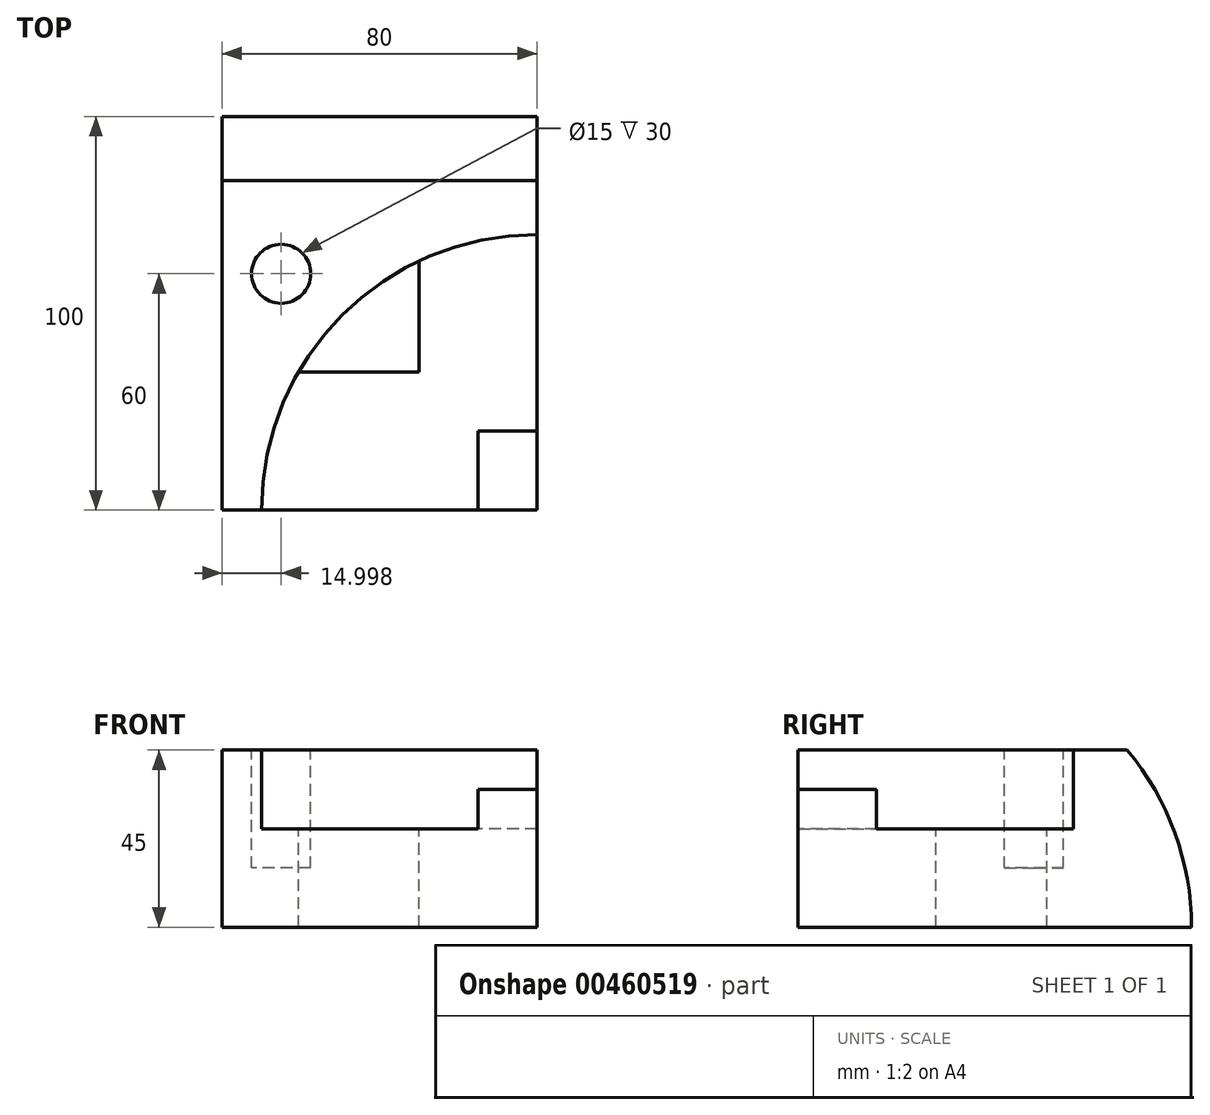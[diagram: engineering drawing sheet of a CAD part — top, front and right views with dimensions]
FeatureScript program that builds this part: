
annotation { "Feature Type Name" : "Feature", "Feature Type Description" : "" }
export const myFeature = defineFeature(function(context is Context, id is Id, definition is map)
    precondition{}
    {
        {
            var Q0;
            Q0=qCreatedBy(makeId("Front.planeOp"),FACE);
            var sketch = newSketch(context, id + "F0", { "sketchPlane" : qUnion([Q0])});
            skLineSegment(sketch, "E0.bottom", {"start": v(-52.62, 0) * mm, "end": v(27.38, 0) * mm});
            skLineSegment(sketch, "E0.top", {"start": v(-52.62, 45) * mm, "end": v(27.38, 45) * mm});
            skLineSegment(sketch, "E0.left", {"start": v(-52.62, 0) * mm, "end": v(-52.62, 45) * mm});
            skLineSegment(sketch, "E0.right", {"start": v(27.38, 0) * mm, "end": v(27.38, 45) * mm});
            skSolve(sketch);
        }
        {
            var Q0;
            Q0=makeQuery(id+"F0.imprint","IMPRINT",FACE,{"disambiguationData":[TD([[makeQuery(id+"F0.imprint","IMPRINT",EDGE,{"derivedFrom":sQuery(id+"F0.wireOp",EDGE,"E0.bottom")}),1.0]])]});
            extrude(context, id + "F1", {"entities" : qUnion([Q0]), "depth" : 100 * mm});
        }
        {
            var Q0;
            Q0=makeQuery(id+"F1.opExtrude","SWEPT_FACE",FACE,{"disambiguationData":[OSD([sQuery(id+"F0.wireOp",EDGE,"E0.right")])]});
            var sketch = newSketch(context, id + "F2", { "sketchPlane" : qUnion([Q0])});
            skLineSegment(sketch, "E1", {"start": v(0, 0) * mm, "end": v(-70, 0) * mm});
            skCircle(sketch, "E2", {"center": v(-70, 0) * mm, "radius": 70 * mm});
            skSolve(sketch);
        }
        {
            var Q0;
            {var subQ1=sQuery(id+"F0.wireOp",EDGE,"E0.right");var subQ2=makeQuery(id+"F1.opExtrude","CAP_EDGE",EDGE,{"disambiguationData":[OSD([subQ1])],"isStart":true});Q0=makeQuery(id+"F2.imprint","IMPRINT",FACE,{"disambiguationData":[TD([[makeQuery(id+"F2.imprint","IMPRINT",EDGE,{"derivedFrom":subQ2}),1.0]])]});}
            extrude(context, id + "F3", {"entities" : qUnion([Q0]), "operationType" : NewBodyOperationType.REMOVE, "oppositeDirection" : true, "depth" : 80 * mm});
        }
        {
            var Q0;
            Q0=makeQuery(id+"F1.opExtrude","SWEPT_FACE",FACE,{"disambiguationData":[OSD([sQuery(id+"F0.wireOp",EDGE,"E0.top")])]});
            var sketch = newSketch(context, id + "F4", { "sketchPlane" : qUnion([Q0])});
            skLineSegment(sketch, "E3", {"start": v(27.38, -100) * mm, "end": v(27.38, -30) * mm});
            skCircle(sketch, "E4", {"center": v(27.38, -100) * mm, "radius": 70 * mm});
            skSolve(sketch);
        }
        {
            var Q0;
            {var subQ0=sQuery(id+"F4.wireOp",EDGE,"E3");Q0=makeQuery(id+"F4.imprint","IMPRINT",FACE,{"disambiguationData":[TD([[makeQuery(id+"F4.imprint","IMPRINT",EDGE,{"derivedFrom":subQ0}),1.0]])]});}
            extrude(context, id + "F5", {"entities" : qUnion([Q0]), "operationType" : NewBodyOperationType.REMOVE, "oppositeDirection" : true, "depth" : 20 * mm});
        }
        {
            var Q0;
            Q0=makeQuery(id+"F5.boolean.opBoolean","COPY",FACE,{"derivedFrom":makeQuery(id+"F5.opExtrude","CAP_FACE",FACE,{"disambiguationData":[OSD([sQuery(id+"F0.wireOp",EDGE,"E0.top"),sQuery(id+"F4.wireOp",EDGE,"E3"),sQuery(id+"F4.wireOp",EDGE,"E4")])],"isStart":false})});
            var sketch = newSketch(context, id + "F6", { "sketchPlane" : qUnion([Q0])});
            skLineSegment(sketch, "E5.bottom", {"start": v(27.38, -100) * mm, "end": v(12.38, -100) * mm});
            skLineSegment(sketch, "E5.top", {"start": v(27.38, -80) * mm, "end": v(12.38, -80) * mm});
            skLineSegment(sketch, "E5.left", {"start": v(27.38, -100) * mm, "end": v(27.38, -80) * mm});
            skLineSegment(sketch, "E5.right", {"start": v(12.38, -100) * mm, "end": v(12.38, -80) * mm});
            skSolve(sketch);
        }
        {
            var Q0;
            Q0=makeQuery(id+"F6.imprint","IMPRINT",FACE,{"disambiguationData":[TD([[makeQuery(id+"F6.imprint","IMPRINT",EDGE,{"derivedFrom":sQuery(id+"F6.wireOp",EDGE,"E5.bottom")}),1.0]])]});
            extrude(context, id + "F7", {"entities" : qUnion([Q0]), "operationType" : NewBodyOperationType.ADD, "depth" : 10 * mm});
        }
        {
            var Q0;
            Q0=makeQuery(id+"F5.boolean.opBoolean","COPY",FACE,{"derivedFrom":makeQuery(id+"F5.opExtrude","CAP_FACE",FACE,{"disambiguationData":[OSD([sQuery(id+"F0.wireOp",EDGE,"E0.top"),sQuery(id+"F4.wireOp",EDGE,"E3"),sQuery(id+"F4.wireOp",EDGE,"E4")])],"isStart":false})});
            var sketch = newSketch(context, id + "F8", { "sketchPlane" : qUnion([Q0])});
            skLineSegment(sketch, "E6", {"start": v(-28.55, -100) * mm, "end": v(-28.55, -65) * mm});
            skLineSegment(sketch, "E7", {"start": v(-28.55, -65) * mm, "end": v(27.38, -65) * mm});
            skLineSegment(sketch, "E8", {"start": v(27.38, -65) * mm, "end": v(-33.24, -65) * mm});
            skLineSegment(sketch, "E9", {"start": v(27.38, -48.43) * mm, "end": v(-2.62, -48.43) * mm});
            skLineSegment(sketch, "E10", {"start": v(-2.62, -48.43) * mm, "end": v(-2.62, -100) * mm});
            skLineSegment(sketch, "E11", {"start": v(-2.62, -100) * mm, "end": v(-2.62, -36.75) * mm});
            skSolve(sketch);
        }
        {
            var Q0;
            {var subQ2=sQuery(id+"F8.wireOp",EDGE,"E8");var subQ4=makeQuery(id+"F8.imprint","INTERSECT",VERTEX,{"derivedFrom":[sQuery(id+"F8.wireOp",EDGE,"E6"),subQ2]});Q0=makeQuery(id+"F8.imprint","IMPRINT",FACE,{"disambiguationData":[TD([[makeQuery(id+"F8.imprint","IMPRINT",EDGE,{"disambiguationData":[TD([[subQ4,1.0]])],"derivedFrom":subQ2}),-1.0]])]});}
            extrude(context, id + "F9", {"entities" : qUnion([Q0]), "operationType" : NewBodyOperationType.REMOVE, "oppositeDirection" : true, "depth" : 25 * mm});
        }
        {
            var Q0;
            Q0=makeQuery(id+"F1.opExtrude","SWEPT_FACE",FACE,{"disambiguationData":[OSD([sQuery(id+"F0.wireOp",EDGE,"E0.top")])]});
            var sketch = newSketch(context, id + "F10", { "sketchPlane" : qUnion([Q0])});
            skLineSegment(sketch, "E12", {"start": v(-52.62, -100) * mm, "end": v(-52.62, -40) * mm});
            skLineSegment(sketch, "E13", {"start": v(27.38, -16.38) * mm, "end": v(-37.62, -16.38) * mm});
            skLineSegment(sketch, "E14.bottom", {"start": v(-37.62, -16.38) * mm, "end": v(-52.62, -16.38) * mm});
            skLineSegment(sketch, "E14.top", {"start": v(-37.62, -40) * mm, "end": v(-52.62, -40) * mm});
            skLineSegment(sketch, "E14.left", {"start": v(-37.62, -16.38) * mm, "end": v(-37.62, -40) * mm});
            skLineSegment(sketch, "E14.right", {"start": v(-52.62, -16.38) * mm, "end": v(-52.62, -40) * mm});
            skCircle(sketch, "E15", {"center": v(-37.62, -40) * mm, "radius": 7.5 * mm});
            skSolve(sketch);
        }
        {
            var Q0;
            {var subQ0=sQuery(id+"F10.wireOp",EDGE,"E14.left");var subQ1=sQuery(id+"F10.wireOp",EDGE,"E14.top");var subQ2=makeQuery(id+"F10.imprint","INTERSECT",VERTEX,{"derivedFrom":[subQ1,subQ0]});Q0=makeQuery(id+"F10.imprint","IMPRINT",FACE,{"disambiguationData":[TD([[makeQuery(id+"F10.imprint","IMPRINT",EDGE,{"disambiguationData":[TD([[subQ2,-1.0]])],"derivedFrom":subQ1}),-1.0]])]});}
            var Q1;
            {var subQ0=sQuery(id+"F10.wireOp",EDGE,"E14.left");var subQ1=sQuery(id+"F10.wireOp",EDGE,"E14.top");var subQ2=makeQuery(id+"F10.imprint","INTERSECT",VERTEX,{"derivedFrom":[subQ1,subQ0]});Q1=makeQuery(id+"F10.imprint","IMPRINT",FACE,{"disambiguationData":[TD([[makeQuery(id+"F10.imprint","IMPRINT",EDGE,{"disambiguationData":[TD([[subQ2,-1.0]])],"derivedFrom":subQ1}),1.0]])]});}
            extrude(context, id + "F11", {"entities" : qUnion([Q0, Q1]), "operationType" : NewBodyOperationType.REMOVE, "oppositeDirection" : true, "depth" : 30 * mm});
        }
    });
